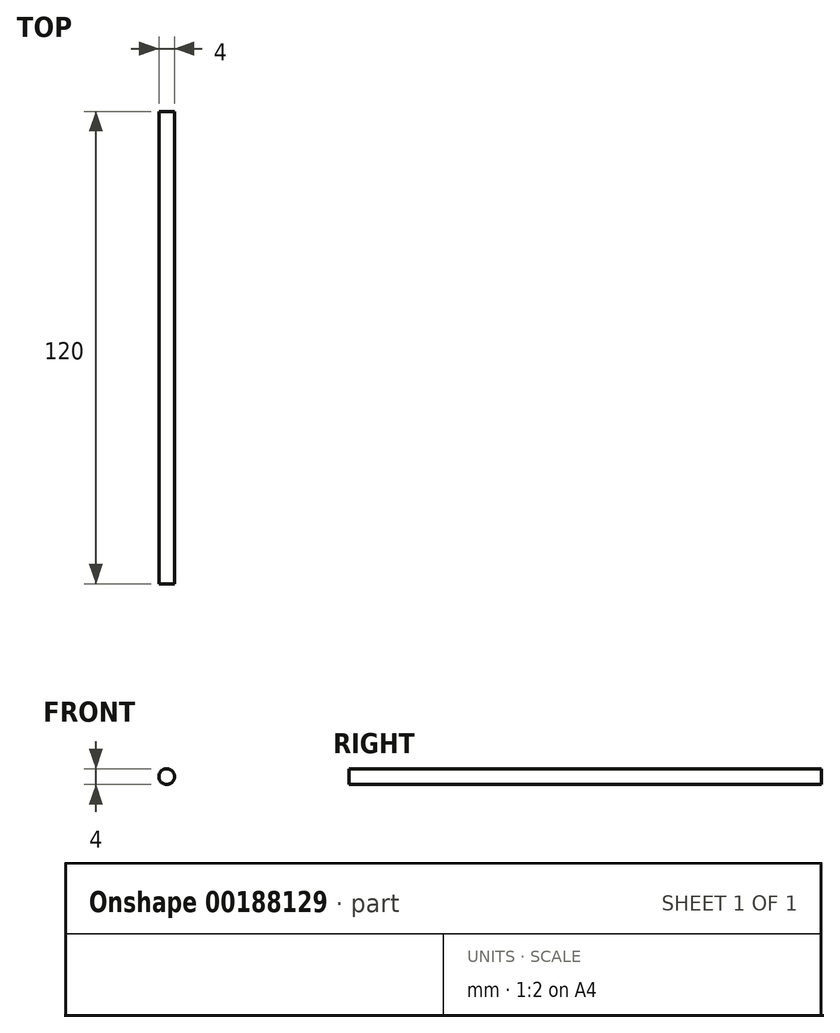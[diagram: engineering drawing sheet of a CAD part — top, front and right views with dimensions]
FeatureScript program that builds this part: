
annotation { "Feature Type Name" : "Feature", "Feature Type Description" : "" }
export const myFeature = defineFeature(function(context is Context, id is Id, definition is map)
    precondition{}
    {
        {
            var Q0;
            Q0=qCreatedBy(makeId("Front.planeOp"),FACE);
            var sketch = newSketch(context, id + "F0", { "sketchPlane" : qUnion([Q0])});
            skCircle(sketch, "E0", {"center": v(0, 0) * mm, "radius": 2 * mm});
            skSolve(sketch);
        }
        {
            var Q0;
            Q0=sQuery(id+"F0.wireOp",EDGE,"E0");
            extrude(context, id + "F1", {"bodyType" : ToolBodyType.SURFACE, "surfaceEntities" : qUnion([Q0]), "depth" : 120 * mm});
        }
    });
